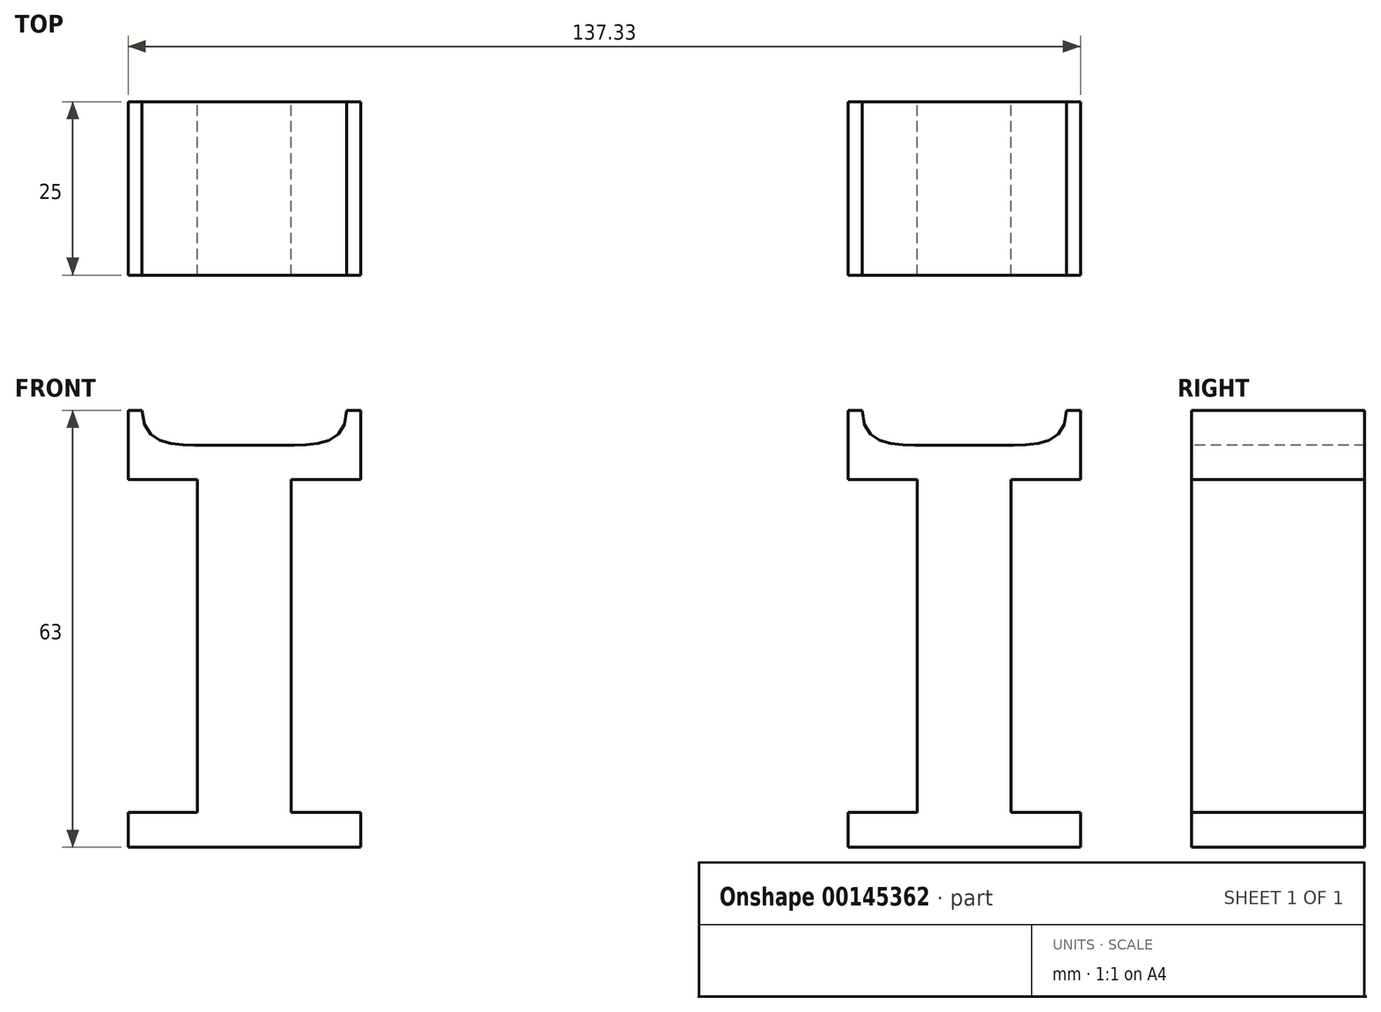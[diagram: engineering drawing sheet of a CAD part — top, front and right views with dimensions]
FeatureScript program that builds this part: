
annotation { "Feature Type Name" : "Feature", "Feature Type Description" : "" }
export const myFeature = defineFeature(function(context is Context, id is Id, definition is map)
    precondition{}
    {
        {
            var Q0;
            Q0=qCreatedBy(makeId("Front.planeOp"),FACE);
            var sketch = newSketch(context, id + "F0", { "sketchPlane" : qUnion([Q0])});
            skLineSegment(sketch, "E0.bottom", {"start": v(-69.15, 32.74) * mm, "end": v(-35.65, 32.74) * mm});
            skLineSegment(sketch, "E0.top", {"start": v(-69.15, -30.26) * mm, "end": v(-35.65, -30.26) * mm});
            skPoint(sketch, "E0.middle", {"position": v(0, 0) * mm});
            skLineSegment(sketch, "E1", {"start": v(34.68, 32.74) * mm, "end": v(34.68, 22.74) * mm});
            skLineSegment(sketch, "E2", {"start": v(34.68, 22.74) * mm, "end": v(68.18, 22.74) * mm});
            skLineSegment(sketch, "E3", {"start": v(68.18, 22.74) * mm, "end": v(68.18, 32.74) * mm});
            skLineSegment(sketch, "E4", {"start": v(-69.15, 32.74) * mm, "end": v(-69.15, 22.74) * mm});
            skLineSegment(sketch, "E5", {"start": v(-69.15, 22.74) * mm, "end": v(-35.65, 22.74) * mm});
            skLineSegment(sketch, "E6", {"start": v(-35.65, 22.74) * mm, "end": v(-35.65, 32.74) * mm});
            skLineSegment(sketch, "E7", {"start": v(44.67, 22.74) * mm, "end": v(44.67, -30.26) * mm});
            skLineSegment(sketch, "E8", {"start": v(58.17, 22.74) * mm, "end": v(58.17, -30.26) * mm});
            skLineSegment(sketch, "E9", {"start": v(-59.15, 22.74) * mm, "end": v(-59.15, -30.26) * mm});
            skLineSegment(sketch, "E10", {"start": v(-45.65, 22.74) * mm, "end": v(-45.65, -30.26) * mm});
            skLineSegment(sketch, "E11.trimOffspring", {"start": v(34.68, 32.74) * mm, "end": v(68.18, 32.74) * mm});
            skLineSegment(sketch, "E12", {"start": v(34.67, -25.26) * mm, "end": v(68.17, -25.26) * mm});
            skLineSegment(sketch, "E13", {"start": v(-69.15, -25.26) * mm, "end": v(-35.65, -25.26) * mm});
            skLineSegment(sketch, "E14.trimOffspring", {"start": v(34.67, -30.26) * mm, "end": v(68.17, -30.26) * mm});
            skLineSegment(sketch, "E15", {"start": v(34.67, -25.26) * mm, "end": v(34.67, -30.26) * mm});
            skLineSegment(sketch, "E16", {"start": v(68.17, -25.26) * mm, "end": v(68.17, -30.26) * mm});
            skLineSegment(sketch, "E17", {"start": v(-35.65, -25.26) * mm, "end": v(-35.65, -30.26) * mm});
            skLineSegment(sketch, "E18", {"start": v(-69.15, -25.26) * mm, "end": v(-69.15, -30.26) * mm});
            skLineSegment(sketch, "E19", {"start": v(-69.15, 27.74) * mm, "end": v(-35.65, 27.74) * mm, "construction": true});
            skLineSegment(sketch, "E20", {"start": v(-59.16, 32.74) * mm, "end": v(-59.15, 22.74) * mm, "construction": true});
            skLineSegment(sketch, "E21", {"start": v(-45.65, 32.74) * mm, "end": v(-45.65, 22.74) * mm, "construction": true});
            skLineSegment(sketch, "E22", {"start": v(-52.4, 32.74) * mm, "end": v(-52.4, 22.74) * mm, "construction": true});
            skLineSegment(sketch, "E23", {"start": v(34.68, 27.74) * mm, "end": v(68.18, 27.74) * mm, "construction": true});
            skLineSegment(sketch, "E24", {"start": v(44.67, 32.74) * mm, "end": v(44.67, 22.74) * mm, "construction": true});
            skLineSegment(sketch, "E25", {"start": v(58.17, 22.74) * mm, "end": v(58.17, 32.74) * mm, "construction": true});
            skLineSegment(sketch, "E26", {"start": v(51.43, 32.74) * mm, "end": v(51.43, 22.74) * mm, "construction": true});
            skLineSegment(sketch, "E27", {"start": v(-67.15, 32.74) * mm, "end": v(-67.15, 22.74) * mm, "construction": true});
            skLineSegment(sketch, "E28", {"start": v(-37.65, 32.74) * mm, "end": v(-37.65, 22.74) * mm, "construction": true});
            skLineSegment(sketch, "E29", {"start": v(36.68, 32.74) * mm, "end": v(36.68, 22.74) * mm, "construction": true});
            skLineSegment(sketch, "E30", {"start": v(66.18, 32.74) * mm, "end": v(66.18, 22.74) * mm, "construction": true});
            skFitSpline(sketch, "E31", {"points": [v(-67.15, 32.74) * mm, v(-59.16, 27.74) * mm, v(-52.4, 27.74) * mm, v(-45.65, 27.74) * mm, v(-37.65, 32.74) * mm], "startDerivative": vector(0, -55.38) * mm, "endDerivative": vector(0, 55.38) * mm});
            skFitSpline(sketch, "E32", {"points": [v(36.68, 32.74) * mm, v(44.67, 27.74) * mm, v(51.43, 27.74) * mm, v(58.17, 27.74) * mm, v(66.18, 32.74) * mm], "startDerivative": vector(0, -55.4) * mm, "endDerivative": vector(0, 55.36) * mm});
            skSolve(sketch);
        }
        {
            var Q0;
            Q0 = qSketchRegion(id + "F0", true);
            extrude(context, id + "F1", {"entities" : qUnion([Q0]), "depth" : 25 * mm});
        }
        {
            var Q0;
            Q0=makeQuery(id+"F1.opExtrude","CAP_FACE",FACE,{"disambiguationData":[OSD([sQuery(id+"F0.wireOp",EDGE,"E0.bottom"),sQuery(id+"F0.wireOp",EDGE,"E0.top"),sQuery(id+"F0.wireOp",EDGE,"E4"),sQuery(id+"F0.wireOp",EDGE,"E5"),sQuery(id+"F0.wireOp",EDGE,"E6"),sQuery(id+"F0.wireOp",EDGE,"E9"),sQuery(id+"F0.wireOp",EDGE,"E10"),sQuery(id+"F0.wireOp",EDGE,"E13"),sQuery(id+"F0.wireOp",EDGE,"E17"),sQuery(id+"F0.wireOp",EDGE,"E18")])],"isStart":false});
            var Q1;
            {var subQ0=sQuery(id+"F0.wireOp",EDGE,"E32");Q1=makeQuery(id+"F0.imprint","IMPRINT",FACE,{"disambiguationData":[TD([[makeQuery(id+"F0.imprint","IMPRINT",EDGE,{"derivedFrom":subQ0}),1.0]])]});}
            var Q2;
            {var subQ0=sQuery(id+"F0.wireOp",EDGE,"E31");Q2=makeQuery(id+"F0.imprint","IMPRINT",FACE,{"disambiguationData":[TD([[makeQuery(id+"F0.imprint","IMPRINT",EDGE,{"derivedFrom":subQ0}),1.0]])]});}
            extrude(context, id + "F2", {"entities" : qUnion([Q0, Q1, Q2]), "operationType" : NewBodyOperationType.REMOVE, "endBound" : BoundingType.THROUGH_ALL, "depth" : 27.75 * mm});
        }
    });
